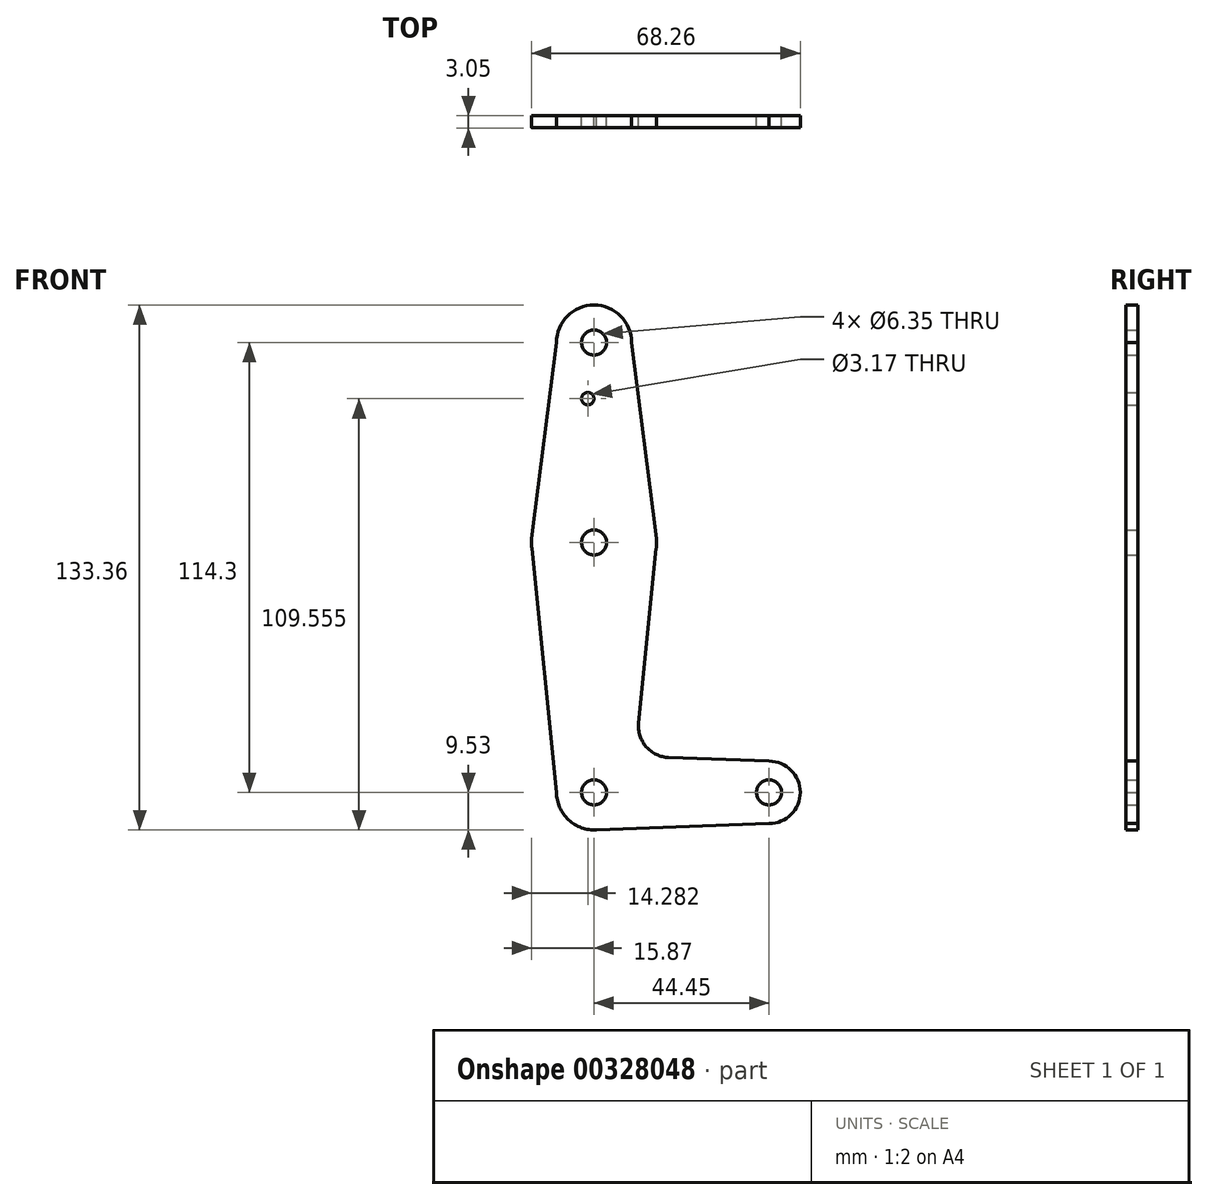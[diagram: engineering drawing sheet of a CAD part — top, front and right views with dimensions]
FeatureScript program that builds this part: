
annotation { "Feature Type Name" : "Feature", "Feature Type Description" : "" }
export const myFeature = defineFeature(function(context is Context, id is Id, definition is map)
    precondition{}
    {
        {
            var Q0;
            Q0=qCreatedBy(makeId("Front.planeOp"),FACE);
            var sketch = newSketch(context, id + "F0", { "sketchPlane" : qUnion([Q0])});
            skLineSegment(sketch, "E0", {"start": v(0, 0) * mm, "end": v(0, 114.3) * mm, "construction": true});
            skLineSegment(sketch, "E1", {"start": v(0, 0) * mm, "end": v(44.45, 0) * mm, "construction": true});
            skCircle(sketch, "E2", {"center": v(44.45, 0) * mm, "radius": 7.94 * mm});
            skCircle(sketch, "E3", {"center": v(0, 0) * mm, "radius": 9.53 * mm});
            skCircle(sketch, "E4", {"center": v(0, 114.3) * mm, "radius": 9.53 * mm});
            skCircle(sketch, "E5", {"center": v(0, 63.5) * mm, "radius": 15.88 * mm});
            skLineSegment(sketch, "E6", {"start": v(44.45, 7.94) * mm, "end": v(18.97, 8.85) * mm});
            skLineSegment(sketch, "E7", {"start": v(-9.53, 114.3) * mm, "end": v(-15.75, 65.5) * mm});
            skLineSegment(sketch, "E8", {"start": v(9.52, 114.3) * mm, "end": v(15.75, 65.5) * mm});
            skLineSegment(sketch, "E9", {"start": v(15.8, 61.91) * mm, "end": v(11.34, 17.6) * mm});
            skCircle(sketch, "E10", {"center": v(0, 0) * mm, "radius": 3.18 * mm});
            skCircle(sketch, "E11", {"center": v(44.45, 0) * mm, "radius": 3.18 * mm});
            skCircle(sketch, "E12", {"center": v(-1.59, 100.03) * mm, "radius": 1.59 * mm});
            skCircle(sketch, "E13", {"center": v(0, 114.3) * mm, "radius": 3.18 * mm});
            skCircle(sketch, "E14", {"center": v(0, 63.5) * mm, "radius": 3.18 * mm});
            skPoint(sketch, "E15.newPointB", {"position": v(0, 9.53) * mm});
            skArc(sketch, "E15.filletArc", {"start": v(11.34, 17.6) * mm, "mid": v(13.26, 11.57) * mm, "end": v(18.97, 8.85) * mm});
            skLineSegment(sketch, "E16", {"start": v(0, -9.52) * mm, "end": v(44.45, -7.94) * mm});
            skLineSegment(sketch, "E17", {"start": v(-9.52, 0) * mm, "end": v(-15.8, 61.91) * mm});
            skSolve(sketch);
        }
        {
            var Q0;
            Q0 = qSketchRegion(id + "F0", true);
            extrude(context, id + "F1", {"entities" : qUnion([Q0]), "depth" : 3.05 * mm});
        }
    });
